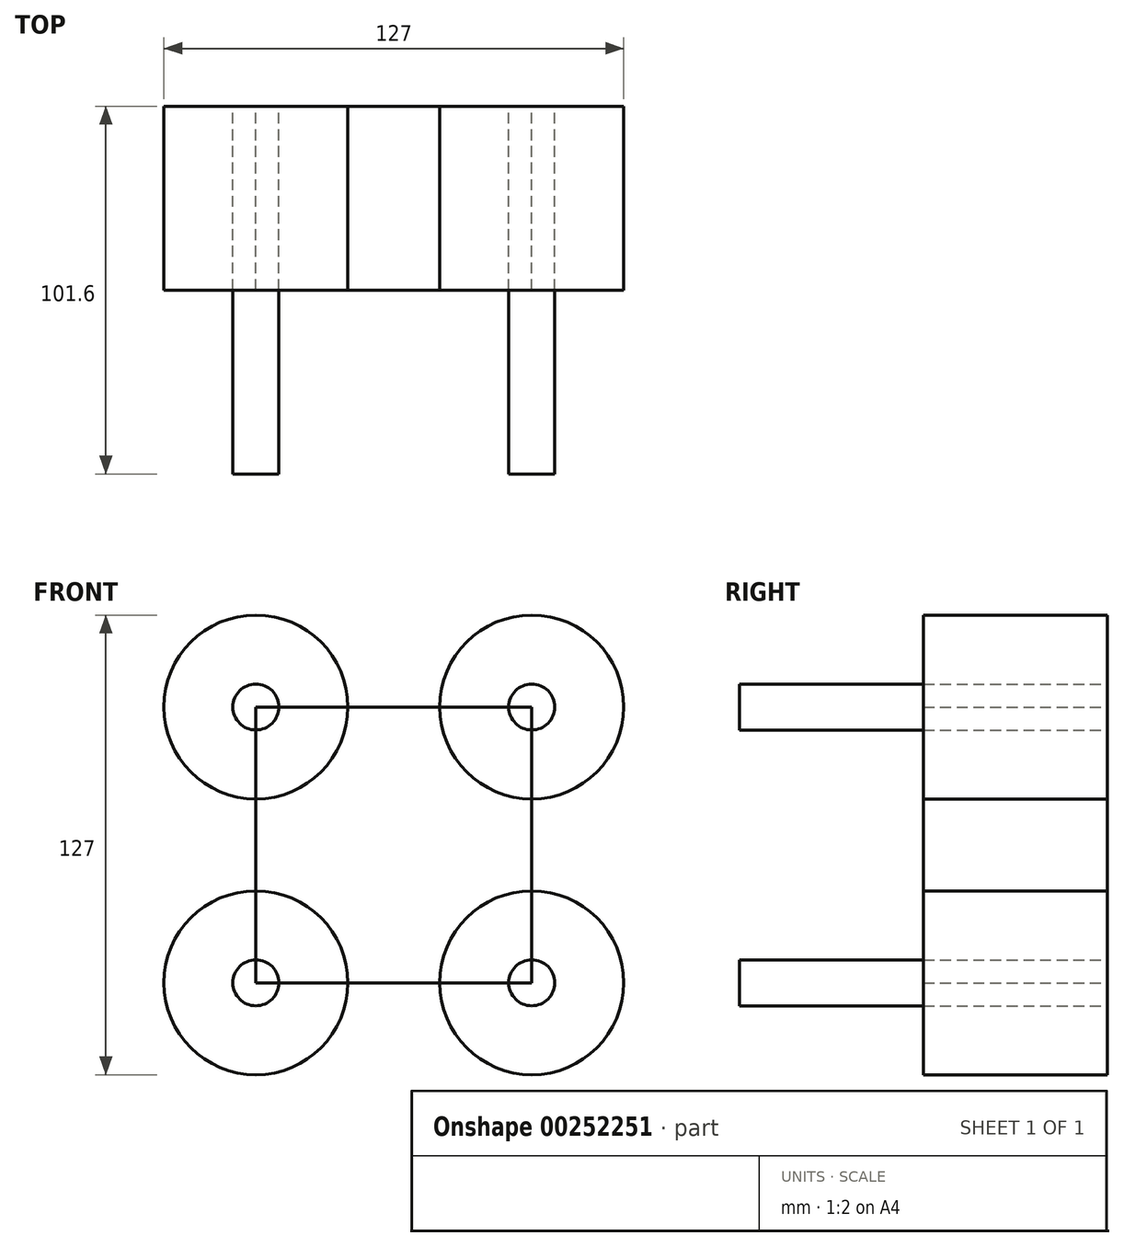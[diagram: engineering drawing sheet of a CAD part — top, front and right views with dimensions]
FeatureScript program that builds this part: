
annotation { "Feature Type Name" : "Feature", "Feature Type Description" : "" }
export const myFeature = defineFeature(function(context is Context, id is Id, definition is map)
    precondition{}
    {
        {
            var Q0;
            Q0=qCreatedBy(makeId("Front.planeOp"),FACE);
            var sketch = newSketch(context, id + "F0", { "sketchPlane" : qUnion([Q0])});
            skLineSegment(sketch, "E0.bottom", {"start": v(38.1, 38.1) * mm, "end": v(-38.1, 38.1) * mm});
            skLineSegment(sketch, "E0.top", {"start": v(38.1, -38.1) * mm, "end": v(-38.1, -38.1) * mm});
            skLineSegment(sketch, "E0.left", {"start": v(38.1, 38.1) * mm, "end": v(38.1, -38.1) * mm});
            skLineSegment(sketch, "E0.right", {"start": v(-38.1, 38.1) * mm, "end": v(-38.1, -38.1) * mm});
            skPoint(sketch, "E0.middle", {"position": v(0, 0) * mm});
            skCircle(sketch, "E1", {"center": v(-38.1, 38.1) * mm, "radius": 25.4 * mm});
            skCircle(sketch, "E2", {"center": v(38.1, 38.1) * mm, "radius": 25.4 * mm});
            skCircle(sketch, "E3", {"center": v(38.1, -38.1) * mm, "radius": 25.4 * mm});
            skCircle(sketch, "E4", {"center": v(-38.1, -38.1) * mm, "radius": 25.4 * mm});
            skCircle(sketch, "E5", {"center": v(-38.1, 38.1) * mm, "radius": 6.35 * mm});
            skCircle(sketch, "E6", {"center": v(38.1, 38.1) * mm, "radius": 6.35 * mm});
            skCircle(sketch, "E7", {"center": v(38.1, -38.1) * mm, "radius": 6.35 * mm});
            skCircle(sketch, "E8", {"center": v(-38.1, -38.1) * mm, "radius": 6.35 * mm});
            skSolve(sketch);
        }
        {
            var Q0;
            {var subQ0=sQuery(id+"F0.wireOp",EDGE,"E2");var subQ13=sQuery(id+"F0.wireOp",EDGE,"E0.bottom");var subQ14=makeQuery(id+"F0.imprint","INTERSECT",VERTEX,{"derivedFrom":[subQ13,subQ0]});Q0=makeQuery(id+"F0.imprint","IMPRINT",FACE,{"disambiguationData":[TD([[makeQuery(id+"F0.imprint","IMPRINT",EDGE,{"disambiguationData":[TD([[subQ14,-1.0]])],"derivedFrom":subQ13}),1.0]])]});}
            var Q1;
            {var subQ0=sQuery(id+"F0.wireOp",EDGE,"E1");var subQ1=sQuery(id+"F0.wireOp",EDGE,"E0.bottom");var subQ2=makeQuery(id+"F0.imprint","INTERSECT",VERTEX,{"derivedFrom":[subQ1,subQ0]});Q1=makeQuery(id+"F0.imprint","IMPRINT",FACE,{"disambiguationData":[TD([[makeQuery(id+"F0.imprint","IMPRINT",EDGE,{"disambiguationData":[TD([[subQ2,-1.0]])],"derivedFrom":subQ1}),-1.0]])]});}
            var Q2;
            {var subQ0=sQuery(id+"F0.wireOp",EDGE,"E2");var subQ1=sQuery(id+"F0.wireOp",EDGE,"E0.bottom");var subQ2=makeQuery(id+"F0.imprint","INTERSECT",VERTEX,{"derivedFrom":[subQ1,subQ0]});Q2=makeQuery(id+"F0.imprint","IMPRINT",FACE,{"disambiguationData":[TD([[makeQuery(id+"F0.imprint","IMPRINT",EDGE,{"disambiguationData":[TD([[subQ2,1.0]])],"derivedFrom":subQ1}),-1.0]])]});}
            var Q3;
            {var subQ0=sQuery(id+"F0.wireOp",EDGE,"E3");var subQ1=sQuery(id+"F0.wireOp",EDGE,"E0.top");var subQ2=makeQuery(id+"F0.imprint","INTERSECT",VERTEX,{"derivedFrom":[subQ1,subQ0]});Q3=makeQuery(id+"F0.imprint","IMPRINT",FACE,{"disambiguationData":[TD([[makeQuery(id+"F0.imprint","IMPRINT",EDGE,{"disambiguationData":[TD([[subQ2,1.0]])],"derivedFrom":subQ1}),1.0]])]});}
            var Q4;
            {var subQ0=sQuery(id+"F0.wireOp",EDGE,"E4");var subQ1=sQuery(id+"F0.wireOp",EDGE,"E0.top");var subQ2=makeQuery(id+"F0.imprint","INTERSECT",VERTEX,{"derivedFrom":[subQ1,subQ0]});Q4=makeQuery(id+"F0.imprint","IMPRINT",FACE,{"disambiguationData":[TD([[makeQuery(id+"F0.imprint","IMPRINT",EDGE,{"disambiguationData":[TD([[subQ2,-1.0]])],"derivedFrom":subQ1}),1.0]])]});}
            extrude(context, id + "F1", {"entities" : qUnion([Q0, Q1, Q2, Q3, Q4]), "depth" : 50.8 * mm});
        }
        {
            var Q0;
            {var subQ0=sQuery(id+"F0.wireOp",EDGE,"E0.right");var subQ1=sQuery(id+"F0.wireOp",EDGE,"E0.bottom");var subQ2=makeQuery(id+"F0.imprint","INTERSECT",VERTEX,{"derivedFrom":[subQ1,subQ0]});Q0=makeQuery(id+"F0.imprint","IMPRINT",FACE,{"disambiguationData":[TD([[makeQuery(id+"F0.imprint","IMPRINT",EDGE,{"disambiguationData":[TD([[subQ2,1.0]])],"derivedFrom":subQ1}),-1.0]])]});}
            var Q1;
            {var subQ0=sQuery(id+"F0.wireOp",EDGE,"E0.left");var subQ1=sQuery(id+"F0.wireOp",EDGE,"E0.bottom");var subQ2=makeQuery(id+"F0.imprint","INTERSECT",VERTEX,{"derivedFrom":[subQ1,subQ0]});Q1=makeQuery(id+"F0.imprint","IMPRINT",FACE,{"disambiguationData":[TD([[makeQuery(id+"F0.imprint","IMPRINT",EDGE,{"disambiguationData":[TD([[subQ2,-1.0]])],"derivedFrom":subQ1}),-1.0]])]});}
            var Q2;
            {var subQ0=sQuery(id+"F0.wireOp",EDGE,"E0.left");var subQ1=sQuery(id+"F0.wireOp",EDGE,"E0.top");var subQ2=makeQuery(id+"F0.imprint","INTERSECT",VERTEX,{"derivedFrom":[subQ1,subQ0]});Q2=makeQuery(id+"F0.imprint","IMPRINT",FACE,{"disambiguationData":[TD([[makeQuery(id+"F0.imprint","IMPRINT",EDGE,{"disambiguationData":[TD([[subQ2,-1.0]])],"derivedFrom":subQ1}),1.0]])]});}
            var Q3;
            {var subQ0=sQuery(id+"F0.wireOp",EDGE,"E0.right");var subQ1=sQuery(id+"F0.wireOp",EDGE,"E0.top");var subQ2=makeQuery(id+"F0.imprint","INTERSECT",VERTEX,{"derivedFrom":[subQ1,subQ0]});Q3=makeQuery(id+"F0.imprint","IMPRINT",FACE,{"disambiguationData":[TD([[makeQuery(id+"F0.imprint","IMPRINT",EDGE,{"disambiguationData":[TD([[subQ2,1.0]])],"derivedFrom":subQ1}),1.0]])]});}
            extrude(context, id + "F2", {"entities" : qUnion([Q0, Q1, Q2, Q3]), "depth" : 101.6 * mm});
        }
        {
            var Q0;
            {var subQ0=sQuery(id+"F0.wireOp",EDGE,"E4");var subQ1=sQuery(id+"F0.wireOp",EDGE,"E0.top");var subQ2=makeQuery(id+"F0.imprint","INTERSECT",VERTEX,{"derivedFrom":[subQ1,subQ0]});Q0=makeQuery(id+"F0.imprint","IMPRINT",FACE,{"disambiguationData":[TD([[makeQuery(id+"F0.imprint","IMPRINT",EDGE,{"disambiguationData":[TD([[subQ2,-1.0]])],"derivedFrom":subQ1}),-1.0]])]});}
            var Q1;
            {var subQ0=sQuery(id+"F0.wireOp",EDGE,"E3");var subQ1=sQuery(id+"F0.wireOp",EDGE,"E0.top");var subQ2=makeQuery(id+"F0.imprint","INTERSECT",VERTEX,{"derivedFrom":[subQ1,subQ0]});Q1=makeQuery(id+"F0.imprint","IMPRINT",FACE,{"disambiguationData":[TD([[makeQuery(id+"F0.imprint","IMPRINT",EDGE,{"disambiguationData":[TD([[subQ2,1.0]])],"derivedFrom":subQ1}),-1.0]])]});}
            var Q2;
            {var subQ0=sQuery(id+"F0.wireOp",EDGE,"E2");var subQ1=sQuery(id+"F0.wireOp",EDGE,"E0.bottom");var subQ2=makeQuery(id+"F0.imprint","INTERSECT",VERTEX,{"derivedFrom":[subQ1,subQ0]});Q2=makeQuery(id+"F0.imprint","IMPRINT",FACE,{"disambiguationData":[TD([[makeQuery(id+"F0.imprint","IMPRINT",EDGE,{"disambiguationData":[TD([[subQ2,1.0]])],"derivedFrom":subQ1}),1.0]])]});}
            var Q3;
            {var subQ0=sQuery(id+"F0.wireOp",EDGE,"E1");var subQ1=sQuery(id+"F0.wireOp",EDGE,"E0.bottom");var subQ2=makeQuery(id+"F0.imprint","INTERSECT",VERTEX,{"derivedFrom":[subQ1,subQ0]});Q3=makeQuery(id+"F0.imprint","IMPRINT",FACE,{"disambiguationData":[TD([[makeQuery(id+"F0.imprint","IMPRINT",EDGE,{"disambiguationData":[TD([[subQ2,-1.0]])],"derivedFrom":subQ1}),1.0]])]});}
            extrude(context, id + "F3", {"entities" : qUnion([Q0, Q1, Q2, Q3]), "depth" : 50.8 * mm});
        }
        {
            var Q0;
            {var subQ0=sQuery(id+"F0.wireOp",EDGE,"E0.right");var subQ1=sQuery(id+"F0.wireOp",EDGE,"E0.bottom");var subQ2=makeQuery(id+"F0.imprint","INTERSECT",VERTEX,{"derivedFrom":[subQ1,subQ0]});Q0=makeQuery(id+"F0.imprint","IMPRINT",FACE,{"disambiguationData":[TD([[makeQuery(id+"F0.imprint","IMPRINT",EDGE,{"disambiguationData":[TD([[subQ2,1.0]])],"derivedFrom":subQ1}),1.0]])]});}
            var Q1;
            {var subQ0=sQuery(id+"F0.wireOp",EDGE,"E0.right");var subQ1=sQuery(id+"F0.wireOp",EDGE,"E0.top");var subQ2=makeQuery(id+"F0.imprint","INTERSECT",VERTEX,{"derivedFrom":[subQ1,subQ0]});Q1=makeQuery(id+"F0.imprint","IMPRINT",FACE,{"disambiguationData":[TD([[makeQuery(id+"F0.imprint","IMPRINT",EDGE,{"disambiguationData":[TD([[subQ2,1.0]])],"derivedFrom":subQ1}),-1.0]])]});}
            var Q2;
            {var subQ0=sQuery(id+"F0.wireOp",EDGE,"E0.left");var subQ1=sQuery(id+"F0.wireOp",EDGE,"E0.top");var subQ2=makeQuery(id+"F0.imprint","INTERSECT",VERTEX,{"derivedFrom":[subQ1,subQ0]});Q2=makeQuery(id+"F0.imprint","IMPRINT",FACE,{"disambiguationData":[TD([[makeQuery(id+"F0.imprint","IMPRINT",EDGE,{"disambiguationData":[TD([[subQ2,-1.0]])],"derivedFrom":subQ1}),-1.0]])]});}
            var Q3;
            {var subQ0=sQuery(id+"F0.wireOp",EDGE,"E0.left");var subQ1=sQuery(id+"F0.wireOp",EDGE,"E0.bottom");var subQ2=makeQuery(id+"F0.imprint","INTERSECT",VERTEX,{"derivedFrom":[subQ1,subQ0]});Q3=makeQuery(id+"F0.imprint","IMPRINT",FACE,{"disambiguationData":[TD([[makeQuery(id+"F0.imprint","IMPRINT",EDGE,{"disambiguationData":[TD([[subQ2,-1.0]])],"derivedFrom":subQ1}),1.0]])]});}
            extrude(context, id + "F4", {"entities" : qUnion([Q0, Q1, Q2, Q3]), "depth" : 101.6 * mm});
        }
    });
